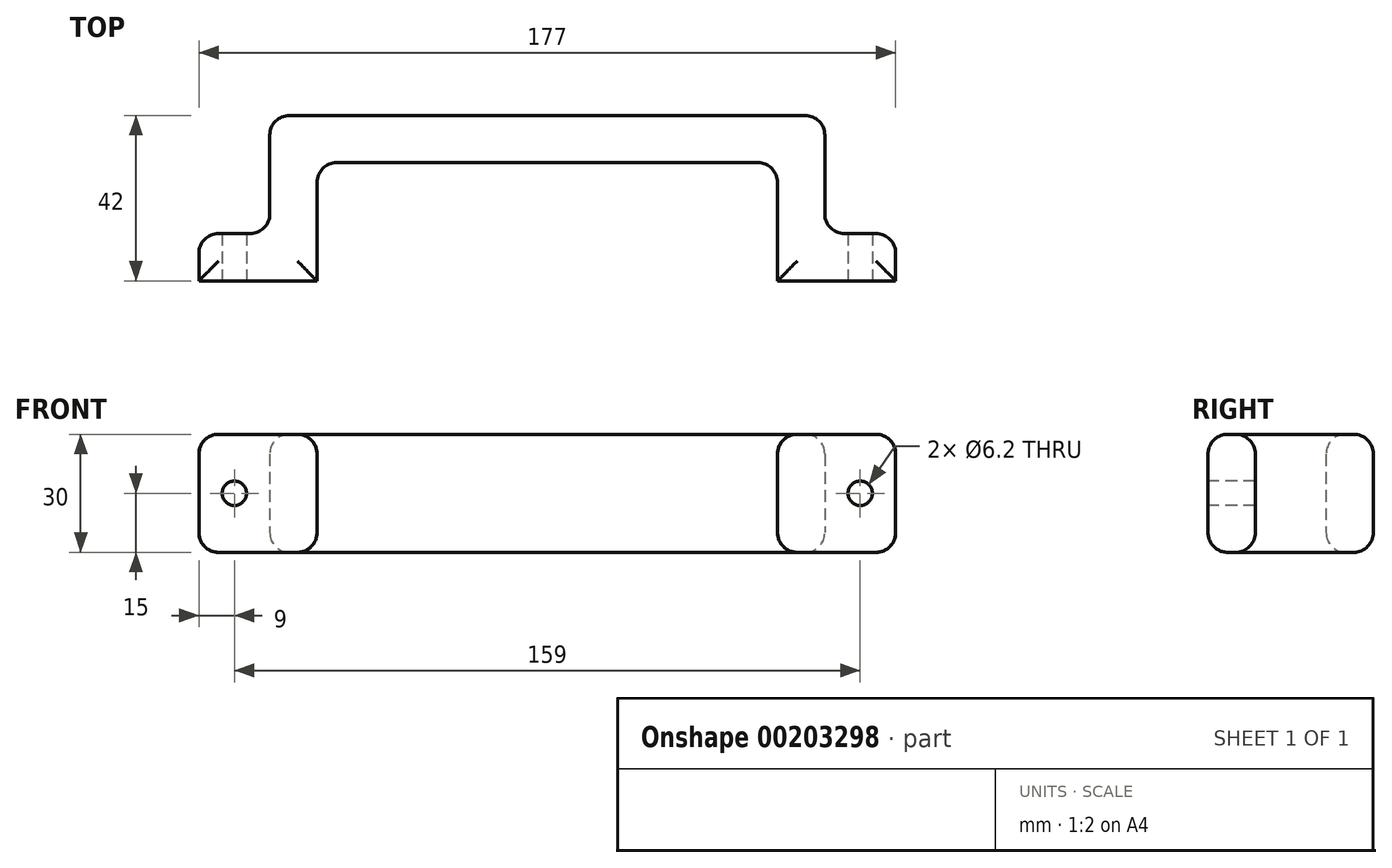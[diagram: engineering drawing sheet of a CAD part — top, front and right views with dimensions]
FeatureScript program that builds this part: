
annotation { "Feature Type Name" : "Feature", "Feature Type Description" : "" }
export const myFeature = defineFeature(function(context is Context, id is Id, definition is map)
    precondition{}
    {
        {
            var Q0;
            Q0=qCreatedBy(makeId("Top.planeOp"),FACE);
            var sketch = newSketch(context, id + "F0", { "sketchPlane" : qUnion([Q0])});
            skLineSegment(sketch, "E0", {"start": v(-88.5, 0) * mm, "end": v(-58.5, 0) * mm});
            skLineSegment(sketch, "E1", {"start": v(-58.5, 0) * mm, "end": v(-58.5, 30) * mm});
            skLineSegment(sketch, "E2", {"start": v(-58.5, 30) * mm, "end": v(58.5, 30) * mm});
            skLineSegment(sketch, "E3", {"start": v(58.5, 30) * mm, "end": v(58.5, 0) * mm});
            skLineSegment(sketch, "E4", {"start": v(58.5, 0) * mm, "end": v(88.5, 0) * mm});
            skLineSegment(sketch, "E5", {"start": v(88.5, 0) * mm, "end": v(88.5, 12) * mm});
            skLineSegment(sketch, "E6", {"start": v(88.5, 12) * mm, "end": v(70.5, 12) * mm});
            skLineSegment(sketch, "E7", {"start": v(70.5, 12) * mm, "end": v(70.5, 42) * mm});
            skLineSegment(sketch, "E8", {"start": v(70.5, 42) * mm, "end": v(-70.5, 42) * mm});
            skLineSegment(sketch, "E9", {"start": v(-70.5, 42) * mm, "end": v(-70.5, 12) * mm});
            skLineSegment(sketch, "E10", {"start": v(-70.5, 12) * mm, "end": v(-88.5, 12) * mm});
            skLineSegment(sketch, "E11", {"start": v(-88.5, 12) * mm, "end": v(-88.5, 0) * mm});
            skSolve(sketch);
        }
        {
            var Q0;
            Q0=makeQuery(id+"F0.imprint","IMPRINT",FACE,{"disambiguationData":[TD([[makeQuery(id+"F0.imprint","IMPRINT",EDGE,{"derivedFrom":sQuery(id+"F0.wireOp",EDGE,"E0")}),1.0]])]});
            extrude(context, id + "F1", {"entities" : qUnion([Q0]), "depth" : 30 * mm});
        }
        {
            var Q0;
            Q0=makeQuery(id+"F1.opExtrude","SWEPT_FACE",FACE,{"disambiguationData":[OSD([sQuery(id+"F0.wireOp",EDGE,"E8")])]});
            var Q1;
            Q1=makeQuery(id+"F1.opExtrude","CAP_FACE",FACE,{"disambiguationData":[OSD([sQuery(id+"F0.wireOp",EDGE,"E0"),sQuery(id+"F0.wireOp",EDGE,"E1"),sQuery(id+"F0.wireOp",EDGE,"E2"),sQuery(id+"F0.wireOp",EDGE,"E3"),sQuery(id+"F0.wireOp",EDGE,"E4"),sQuery(id+"F0.wireOp",EDGE,"E5"),sQuery(id+"F0.wireOp",EDGE,"E6"),sQuery(id+"F0.wireOp",EDGE,"E7"),sQuery(id+"F0.wireOp",EDGE,"E8"),sQuery(id+"F0.wireOp",EDGE,"E9"),sQuery(id+"F0.wireOp",EDGE,"E10"),sQuery(id+"F0.wireOp",EDGE,"E11")])],"isStart":false});
            var Q2;
            Q2=makeQuery(id+"F1.opExtrude","CAP_FACE",FACE,{"disambiguationData":[OSD([sQuery(id+"F0.wireOp",EDGE,"E0"),sQuery(id+"F0.wireOp",EDGE,"E1"),sQuery(id+"F0.wireOp",EDGE,"E2"),sQuery(id+"F0.wireOp",EDGE,"E3"),sQuery(id+"F0.wireOp",EDGE,"E4"),sQuery(id+"F0.wireOp",EDGE,"E5"),sQuery(id+"F0.wireOp",EDGE,"E6"),sQuery(id+"F0.wireOp",EDGE,"E7"),sQuery(id+"F0.wireOp",EDGE,"E8"),sQuery(id+"F0.wireOp",EDGE,"E9"),sQuery(id+"F0.wireOp",EDGE,"E10"),sQuery(id+"F0.wireOp",EDGE,"E11")])],"isStart":true});
            var Q3;
            Q3=makeQuery(id+"F1.opExtrude","SWEPT_EDGE",EDGE,{"disambiguationData":[OSD([sQuery(id+"F0.wireOp",EDGE,"E6"),sQuery(id+"F0.wireOp",EDGE,"E7")])]});
            var Q4;
            Q4=makeQuery(id+"F1.opExtrude","SWEPT_EDGE",EDGE,{"disambiguationData":[OSD([sQuery(id+"F0.wireOp",EDGE,"E9"),sQuery(id+"F0.wireOp",EDGE,"E10")])]});
            var Q5;
            Q5=makeQuery(id+"F1.opExtrude","SWEPT_EDGE",EDGE,{"disambiguationData":[OSD([sQuery(id+"F0.wireOp",EDGE,"E1"),sQuery(id+"F0.wireOp",EDGE,"E2")])]});
            var Q6;
            Q6=makeQuery(id+"F1.opExtrude","SWEPT_EDGE",EDGE,{"disambiguationData":[OSD([sQuery(id+"F0.wireOp",EDGE,"E2"),sQuery(id+"F0.wireOp",EDGE,"E3")])]});
            var Q7;
            Q7=makeQuery(id+"F1.opExtrude","SWEPT_EDGE",EDGE,{"disambiguationData":[OSD([sQuery(id+"F0.wireOp",EDGE,"E10"),sQuery(id+"F0.wireOp",EDGE,"E11")])]});
            var Q8;
            Q8=makeQuery(id+"F1.opExtrude","SWEPT_EDGE",EDGE,{"disambiguationData":[OSD([sQuery(id+"F0.wireOp",EDGE,"E5"),sQuery(id+"F0.wireOp",EDGE,"E6")])]});
            fillet(context, id + "F2", {"entities" : qUnion([Q0, Q1, Q2, Q3, Q4, Q5, Q6, Q7, Q8]), "radius" : 5 * mm, "tangentPropagation" : true, "allowEdgeOverflow" : false});
        }
        {
            var Q0;
            Q0=makeQuery(id+"F1.opExtrude","SWEPT_FACE",FACE,{"disambiguationData":[OSD([sQuery(id+"F0.wireOp",EDGE,"E0")])]});
            var sketch = newSketch(context, id + "F3", { "sketchPlane" : qUnion([Q0])});
            skCircle(sketch, "E12", {"center": v(-79.5, 15) * mm, "radius": 3.1 * mm});
            skCircle(sketch, "E13", {"center": v(79.5, 15) * mm, "radius": 3.1 * mm});
            skSolve(sketch);
        }
        {
            var Q0;
            Q0=makeQuery(id+"F3.imprint","IMPRINT",FACE,{"disambiguationData":[TD([[makeQuery(id+"F3.imprint","IMPRINT",EDGE,{"derivedFrom":sQuery(id+"F3.wireOp",EDGE,"E13")}),1.0]])]});
            var Q1;
            Q1=makeQuery(id+"F3.imprint","IMPRINT",FACE,{"disambiguationData":[TD([[makeQuery(id+"F3.imprint","IMPRINT",EDGE,{"derivedFrom":sQuery(id+"F3.wireOp",EDGE,"E12")}),1.0]])]});
            extrude(context, id + "F4", {"entities" : qUnion([Q0, Q1]), "operationType" : NewBodyOperationType.REMOVE, "oppositeDirection" : true, "depth" : 25 * mm});
        }
    });
